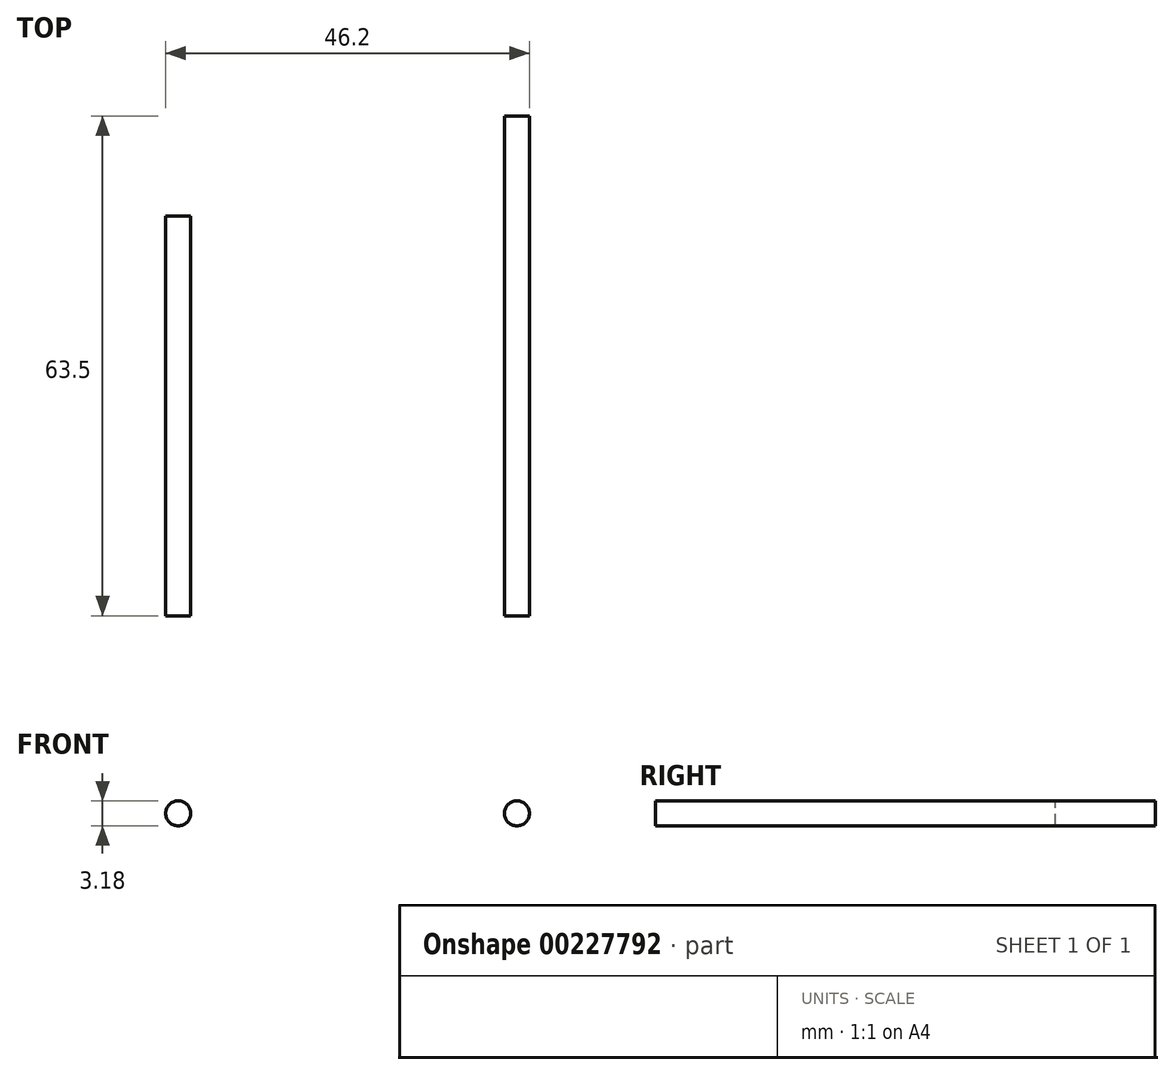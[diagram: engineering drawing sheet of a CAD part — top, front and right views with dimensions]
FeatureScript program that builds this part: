
annotation { "Feature Type Name" : "Feature", "Feature Type Description" : "" }
export const myFeature = defineFeature(function(context is Context, id is Id, definition is map)
    precondition{}
    {
        {
            var Q0;
            Q0=qCreatedBy(makeId("Front.planeOp"),FACE);
            var sketch = newSketch(context, id + "F0", { "sketchPlane" : qUnion([Q0])});
            skCircle(sketch, "E0", {"center": v(-24.17, 0) * mm, "radius": 1.59 * mm});
            skCircle(sketch, "E1", {"center": v(18.85, 0) * mm, "radius": 1.59 * mm});
            skSolve(sketch);
        }
        {
            var Q0;
            Q0=qSketchRegion(id+"F0",true);
            extrude(context, id + "F1", {"entities" : qUnion([Q0]), "depth" : 50.8 * mm});
        }
        {
            var Q0;
            Q0=makeQuery(id+"F1.opExtrude","CAP_FACE",FACE,{"disambiguationData":[OSD([sQuery(id+"F0.wireOp",EDGE,"E1")])],"isStart":true});
            extrude(context, id + "F2", {"entities" : qUnion([Q0]), "operationType" : NewBodyOperationType.ADD, "depth" : 12.7 * mm});
        }
    });
